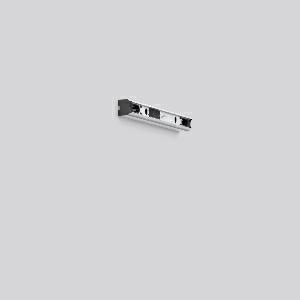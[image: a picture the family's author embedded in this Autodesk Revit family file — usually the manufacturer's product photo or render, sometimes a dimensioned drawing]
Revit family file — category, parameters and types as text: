
# Revit family: alu-stableuchten_41530_004_7568
name_source: partatom
category: Lighting Fixtures
units: mm (PartAtom-declared; Revit-internal decimal feet)

## family parameters
Cut with Voids When Loaded = No
Host = Face
Light Source = No
Part Type = Normal
Room Calculation Point = No
Round Connector Dimension = Use Diameter
Shared = No

## types (1)
- ALU-Stableuchten (1 x LED L S14S, 1000 lm, 16 W, 2700)
    Apparent Load = 16 VA
    CIE Flux Codes = 34 61 82 75 81
    Color Rendering = 80
    Color Temperature = 2700
    Default Elevation = 1800 mm
    Description = Series: Aluminium striplights
Aluminium striplight for linear lamps. Base: extruded anodised aluminium profile. End caps: plastic. Lamp contacts disconnection during lamp replacement. Light source must be ordered separately. 
Colour: anodised aluminium
Length: 300 mm
Width: 35 mm
Height: 58 mm
Lamp: L-DE
Number of lamps: 1
Wattage: 35 W
Socket: S14s
System power: 30 W
Rated luminous flux: 1100 lm
Luminous efficiency: 37 lm/W
Control gear: Converter not necessary
Protection class: I
Type of protection: IP 40
    Height = 58 mm
    Lamp = 1 x LED L S14S
    Lamp Light Flux = 1000 lm
    Lamp Power = 16 W
    Lamp count = 1
    Length = 300 mm
    Lifetime = 25000 h
    Luminous efficacy = 51 lm/W
    Manufacturer = RZB
    ModVariant = No
    Model = 41530.004
    Mounting Place = Ceiling, Wall
    Mounting Type = Surface mounted
    Number of Poles = 1
    OnlyDefault = Yes
    Power Factor = 1
    Product Name = ALU-Stableuchten
    Product group = Surface mounted ceiling and wall luminaires
    ProductGroupID = 305
    Protection Class = Protection class I
    Protection Degree = IP 40
    RLX_Detail_Level = 1
    RLX_Emergency_Light_Flux = 0 lm
    RLX_Emergency_Type = 0
    RLX_Emergency_Type_DB = No
    RlxData = <blob elided: 11741 chars, md5=441b9933>
    Socket = S14s
    Standby Power = 0 W
    System Light Flux = 813 lm
    System Power = 16 W
    Type Comments = Product without accessories
    Type Image = 41530.004.jpg
    URL = http://relux.com
    VarID = ---
    Voltage = 230 V
    Voltage Range = 220-240 V
    Weight = 0.00 kg
    Width = 35 mm

## geometry (parser evidence)
native form markers: Sweep x10
no freeform markers — native parametric forms only
